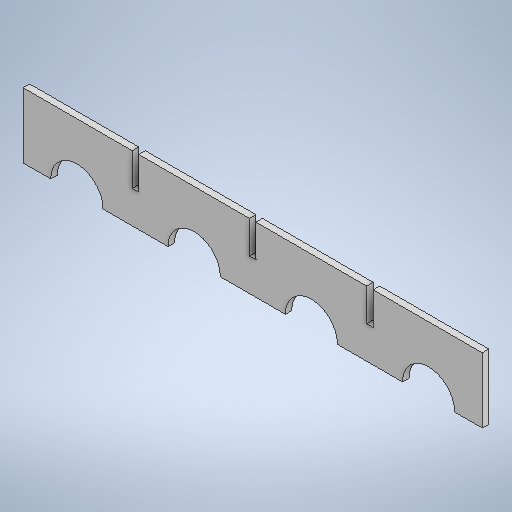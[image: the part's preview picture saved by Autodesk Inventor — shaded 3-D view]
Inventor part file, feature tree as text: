
AUTODESK INVENTOR PART (.ipt)
format: ipt  version: 2025 (Build 290162010, 162A)  size: 296,960 bytes
history: native  units: mm
features: extrude x2, sketch x2
ambient origin geometry x8: Origin, YZ Plane, XZ Plane, XY Plane, X Axis, Y Axis, Z Axis, Center Point
bodies: Solid1 (feature_tree)
feature tree (4):
  extrude  "Extrusion1"  Depth=100.0mm TaperAngle=0.0deg
  extrude  "Extrusion3"  Depth=180.0mm
  sketch  "Sketch1"  dims[d0=800.0mm d3=100.0mm d4=0.0mm]
  sketch  "Sketch3"  dims[d24=10.0mm d25=180.0mm d26=705.0mm d59=80.0mm d60=80.0mm d61=90.0mm d62=180.0mm d63=80.0mm d64=90.0mm d65=80.0mm d66=180.0mm d67=10.0mm d68=50.0mm d69=180.0mm d70=10.0mm d71=50.0mm d72=180.0mm d73=50.0mm d74=10.0mm d75=0.0mm d76=0.0mm]
